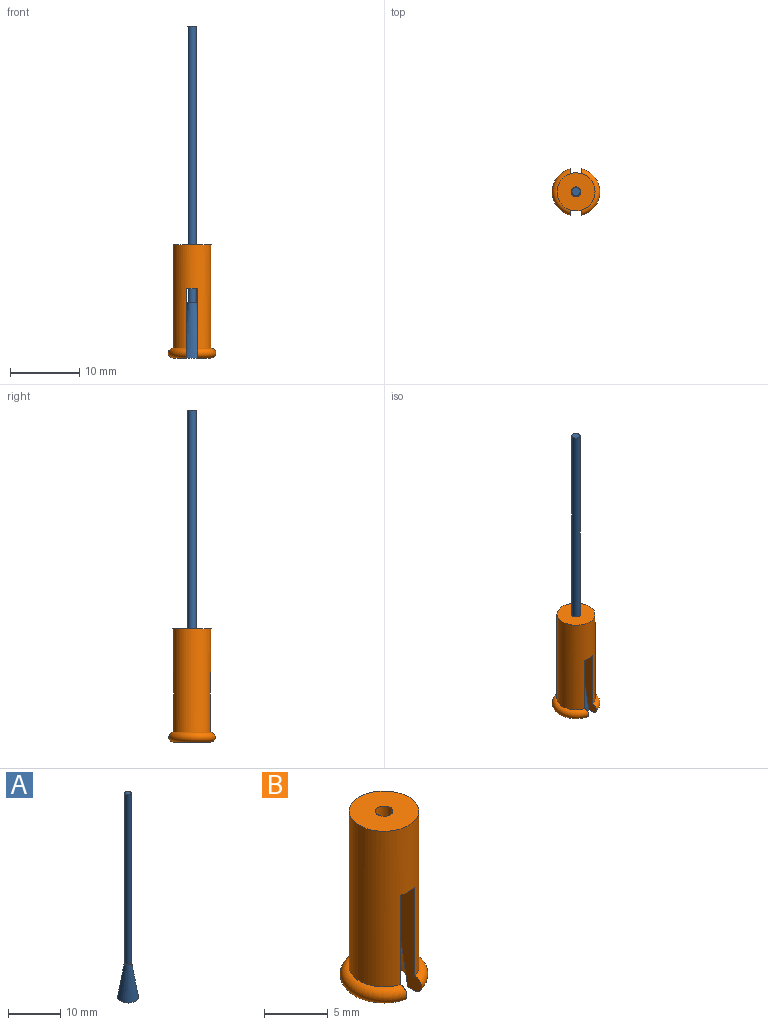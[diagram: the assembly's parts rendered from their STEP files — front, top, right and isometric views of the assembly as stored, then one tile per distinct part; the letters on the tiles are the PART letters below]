
ASSEMBLY  parts=2 mates=1
PART A: 5 faces, bbox 4x4x48 mm
  f0: plane 4x4mm, normal (0,0,-1), area 12.6mm2, adj f1
  f1: cone r=2mm half-angle=9.2deg, axis (0,0,-1), area 68.7mm2, adj f0,f2
  f2: plane 1.4x1.4mm, normal (0,0,1), area 0.4mm2, adj f1,f3
  f3: cylinder r=0.6mm len=40mm, axis (0,0,-1), area 150.8mm2, adj f2,f4
  f4: plane 1.2x1.2mm, normal (0,0,1), area 1.1mm2, adj f3
PART B: 12 faces, bbox 7.5x7.3x16.4 mm
  f0: torus R=2.75mm, axis (0,0,1), area 18.5mm2, adj f2,f6,f9
  f1: plane 5.26x1.95mm, normal (0,0,-1), area 4.4mm2, adj f5,f8,f10
  f2: cylinder r=2.75mm len=15mm, axis (0,0,-1), area 231.3mm2, adj f0,f5,f7,f9,f10,f11
  f3: cone r=0.7mm half-angle=9.2deg, axis (0,0,-1), area 19.7mm2, adj f6,f9
  f4: cylinder r=0.7mm len=6.4mm, axis (0,0,1), area 28.1mm2, adj f7,f11
  f5: torus R=2.75mm, axis (0,0,1), area 18.5mm2, adj f1,f2,f10
  f6: plane 5.26x1.95mm, normal (0,0,-1), area 4.4mm2, adj f0,f3,f9
  f7: plane 5.5x5.5mm, normal (0,0,1), area 22.2mm2, adj f2,f4
  f8: cone r=0.7mm half-angle=9.2deg, axis (0,0,-1), area 19.8mm2, adj f1,f10
  f9: plane 10x6.71mm, normal (1,0,0), area 37.9mm2, adj f0,f2,f3,f6,f11
  f10: plane 10x6.71mm, normal (-1,0,0), area 37.9mm2, adj f1,f2,f5,f8,f11
  f11: plane 5.5x1.6mm, normal (0,0,-1), area 7.1mm2, adj f2,f4,f9,f10
PLACE A t=(-0.99,2.2,-1.54)mm
PLACE B t=(-0.99,2.2,-0.84)mm
MATE fastened A.f1 <-> B.f0  axis (0,0,-1) through (-0.99,2.2,-1.54)mm
